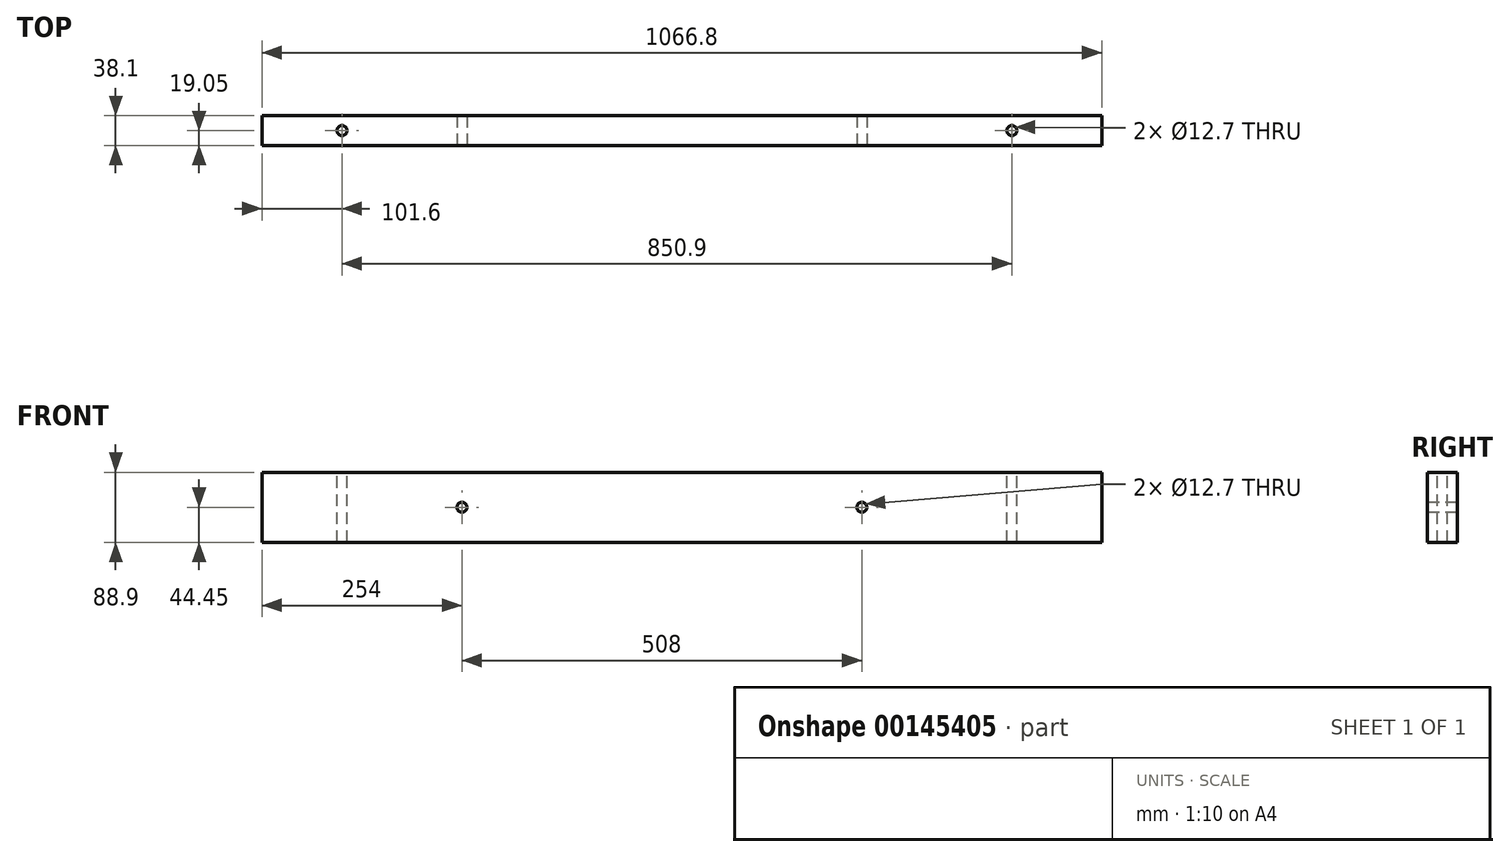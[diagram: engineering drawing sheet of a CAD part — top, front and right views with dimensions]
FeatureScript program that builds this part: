
annotation { "Feature Type Name" : "Feature", "Feature Type Description" : "" }
export const myFeature = defineFeature(function(context is Context, id is Id, definition is map)
    precondition{}
    {
        {
            var Q0;
            Q0=qCreatedBy(makeId("Front.planeOp"),FACE);
            var sketch = newSketch(context, id + "F0", { "sketchPlane" : qUnion([Q0])});
            skLineSegment(sketch, "E0.bottom", {"start": v(-533.4, -44.45) * mm, "end": v(533.4, -44.45) * mm});
            skLineSegment(sketch, "E0.top", {"start": v(-533.4, 44.45) * mm, "end": v(533.4, 44.45) * mm});
            skLineSegment(sketch, "E0.left", {"start": v(-533.4, -44.45) * mm, "end": v(-533.4, 44.45) * mm});
            skLineSegment(sketch, "E0.right", {"start": v(533.4, -44.45) * mm, "end": v(533.4, 44.45) * mm});
            skPoint(sketch, "E0.middle", {"position": v(0, 0) * mm});
            skPoint(sketch, "E1", {"position": v(-381, 0) * mm});
            skSolve(sketch);
        }
        {
            var Q0;
            Q0 = qSketchRegion(id + "F0", true);
            extrude(context, id + "F1", {"entities" : qUnion([Q0]), "endBound" : BoundingType.SYMMETRIC, "depth" : 38.1 * mm});
        }
        {
            var Q0;
            Q0=makeQuery(id+"F1.opExtrude","SWEPT_BODY",BODY,{"disambiguationData":[OSD([sQuery(id+"F0.wireOp",EDGE,"E0.bottom"),sQuery(id+"F0.wireOp",EDGE,"E0.top"),sQuery(id+"F0.wireOp",EDGE,"E0.left"),sQuery(id+"F0.wireOp",EDGE,"E0.right")])]});
            transform(context, id + "F2", {"entities" : qUnion([Q0]), "transformType" : TransformType.TRANSLATION_3D, "dx" : 0 * mm, "dy" : 114.3 * mm, "dz" : 0 * mm, "makeCopy" : true});
        }
        {
            var Q0;
            Q0=qCreatedBy(makeId("Front.planeOp"),FACE);
            var sketch = newSketch(context, id + "F3", { "sketchPlane" : qUnion([Q0])});
            skLineSegment(sketch, "E2.bottom", {"start": v(-190.5, 44.45) * mm, "end": v(190.5, 44.45) * mm});
            skLineSegment(sketch, "E2.top", {"start": v(-190.5, -44.45) * mm, "end": v(190.5, -44.45) * mm});
            skLineSegment(sketch, "E2.left", {"start": v(-190.5, 44.45) * mm, "end": v(-190.5, -44.45) * mm});
            skLineSegment(sketch, "E2.right", {"start": v(190.5, 44.45) * mm, "end": v(190.5, -44.45) * mm});
            skPoint(sketch, "E2.middle", {"position": v(0, 0) * mm});
            skSolve(sketch);
        }
        {
            var Q0;
            Q0 = qSketchRegion(id + "F3", true);
            extrude(context, id + "F4", {"entities" : qUnion([Q0]), "operationType" : NewBodyOperationType.ADD, "endBound" : BoundingType.SYMMETRIC, "depth" : 38.1 * mm});
        }
        {
            var Q0;
            Q0=makeQuery(id+"F2.opPattern","COPY",BODY,{"derivedFrom":makeQuery(id+"F1.opExtrude","SWEPT_BODY",BODY,{"disambiguationData":[OSD([sQuery(id+"F0.wireOp",EDGE,"E0.bottom"),sQuery(id+"F0.wireOp",EDGE,"E0.top"),sQuery(id+"F0.wireOp",EDGE,"E0.left"),sQuery(id+"F0.wireOp",EDGE,"E0.right")])]}),"instanceName":"1"});
            deleteBodies(context, id + "F5", {"entities" : qUnion([Q0])});
        }
        {
            var Q0;
            Q0=makeQuery(id+"F1.opExtrude","SWEPT_BODY",BODY,{"disambiguationData":[OSD([sQuery(id+"F0.wireOp",EDGE,"E0.bottom"),sQuery(id+"F0.wireOp",EDGE,"E0.top"),sQuery(id+"F0.wireOp",EDGE,"E0.left"),sQuery(id+"F0.wireOp",EDGE,"E0.right")])]});
            transform(context, id + "F6", {"entities" : qUnion([Q0]), "transformType" : TransformType.TRANSLATION_3D, "dx" : 0 * mm, "dy" : 152.4 * mm, "dz" : 0 * mm, "makeCopy" : true});
        }
        {
            var Q0;
            Q0=qCreatedBy(makeId("Front.planeOp"),FACE);
            cPlane(context, id + "F7", {"entities" : qUnion([Q0]), "cplaneType" : CPlaneType.OFFSET, "offset" : 91.44 * mm, "width" : 152.4 * mm, "height" : 152.4 * mm});
        }
        {
            var Q0;
            Q0=qCreatedBy(makeId("Top.planeOp"),FACE);
            cPlane(context, id + "F8", {"entities" : qUnion([Q0]), "cplaneType" : CPlaneType.OFFSET, "offset" : 152.4 * mm, "width" : 152.4 * mm, "height" : 152.4 * mm});
        }
        {
            var Q0;
            Q0=qCreatedBy(id+"F8.planeOp",FACE);
            var sketch = newSketch(context, id + "F9", { "sketchPlane" : qUnion([Q0])});
            skPoint(sketch, "E3", {"position": v(419.1, 0) * mm});
            skPoint(sketch, "E4", {"position": v(419.1, 152.4) * mm});
            skSolve(sketch);
        }
        {
            var Q0;
            Q0=sQuery(id+"F9.wireOp",VERTEX,"E4");
            var Q1;
            Q1=makeQuery(id+"F6.opPattern","COPY",BODY,{"derivedFrom":makeQuery(id+"F1.opExtrude","SWEPT_BODY",BODY,{"disambiguationData":[OSD([sQuery(id+"F0.wireOp",EDGE,"E0.bottom"),sQuery(id+"F0.wireOp",EDGE,"E0.top"),sQuery(id+"F0.wireOp",EDGE,"E0.left"),sQuery(id+"F0.wireOp",EDGE,"E0.right")])]}),"instanceName":"1"});
            hole(context, id + "F10", {"style" : HoleStyle.SIMPLE, "endStyle" : HoleEndStyle.BLIND, "holeDiameter" : 12.7 * mm, "holeDepth" : 609.6 * mm, "startFromSketch" : true, "locations" : qUnion([Q0]), "scope" : qUnion([Q1])});
        }
        {
            var Q0;
            Q0=sQuery(id+"F9.wireOp",VERTEX,"E3");
            var Q1;
            Q1=makeQuery(id+"F1.opExtrude","SWEPT_BODY",BODY,{"disambiguationData":[OSD([sQuery(id+"F0.wireOp",EDGE,"E0.bottom"),sQuery(id+"F0.wireOp",EDGE,"E0.top"),sQuery(id+"F0.wireOp",EDGE,"E0.left"),sQuery(id+"F0.wireOp",EDGE,"E0.right")])]});
            hole(context, id + "F11", {"style" : HoleStyle.SIMPLE, "endStyle" : HoleEndStyle.BLIND, "holeDiameter" : 12.7 * mm, "holeDepth" : 609.6 * mm, "startFromSketch" : true, "locations" : qUnion([Q0]), "scope" : qUnion([Q1])});
        }
        {
            var Q0;
            Q0=qCreatedBy(id+"F7.planeOp",FACE);
            var sketch = newSketch(context, id + "F12", { "sketchPlane" : qUnion([Q0])});
            skPoint(sketch, "E5", {"position": v(-279.4, 0) * mm});
            skSolve(sketch);
        }
        {
            var Q0;
            Q0=sQuery(id+"F12.wireOp",VERTEX,"E5");
            var Q1;
            Q1=makeQuery(id+"F1.opExtrude","SWEPT_BODY",BODY,{"disambiguationData":[OSD([sQuery(id+"F0.wireOp",EDGE,"E0.bottom"),sQuery(id+"F0.wireOp",EDGE,"E0.top"),sQuery(id+"F0.wireOp",EDGE,"E0.left"),sQuery(id+"F0.wireOp",EDGE,"E0.right")])]});
            var Q2;
            Q2=makeQuery(id+"F6.opPattern","COPY",BODY,{"derivedFrom":makeQuery(id+"F1.opExtrude","SWEPT_BODY",BODY,{"disambiguationData":[OSD([sQuery(id+"F0.wireOp",EDGE,"E0.bottom"),sQuery(id+"F0.wireOp",EDGE,"E0.top"),sQuery(id+"F0.wireOp",EDGE,"E0.left"),sQuery(id+"F0.wireOp",EDGE,"E0.right")])]}),"instanceName":"1"});
            hole(context, id + "F13", {"style" : HoleStyle.SIMPLE, "endStyle" : HoleEndStyle.BLIND, "holeDiameter" : 12.7 * mm, "holeDepth" : 609.6 * mm, "startFromSketch" : true, "locations" : qUnion([Q0]), "scope" : qUnion([Q1, Q2])});
        }
        {
            var Q0;
            Q0=makeQuery(id+"F6.opPattern","COPY",BODY,{"derivedFrom":makeQuery(id+"F1.opExtrude","SWEPT_BODY",BODY,{"disambiguationData":[OSD([sQuery(id+"F0.wireOp",EDGE,"E0.bottom"),sQuery(id+"F0.wireOp",EDGE,"E0.top"),sQuery(id+"F0.wireOp",EDGE,"E0.left"),sQuery(id+"F0.wireOp",EDGE,"E0.right")])]}),"instanceName":"1"});
            deleteBodies(context, id + "F14", {"entities" : qUnion([Q0])});
        }
        {
            var Q0;
            Q0=qCreatedBy(id+"F8.planeOp",FACE);
            var sketch = newSketch(context, id + "F15", { "sketchPlane" : qUnion([Q0])});
            skPoint(sketch, "E6", {"position": v(-431.8, 0) * mm});
            skSolve(sketch);
        }
        {
            var Q0;
            Q0=sQuery(id+"F15.wireOp",VERTEX,"E6");
            var Q1;
            Q1=makeQuery(id+"F1.opExtrude","SWEPT_BODY",BODY,{"disambiguationData":[OSD([sQuery(id+"F0.wireOp",EDGE,"E0.bottom"),sQuery(id+"F0.wireOp",EDGE,"E0.top"),sQuery(id+"F0.wireOp",EDGE,"E0.left"),sQuery(id+"F0.wireOp",EDGE,"E0.right")])]});
            hole(context, id + "F16", {"style" : HoleStyle.SIMPLE, "endStyle" : HoleEndStyle.BLIND, "holeDiameter" : 12.7 * mm, "holeDepth" : 609.6 * mm, "locations" : qUnion([Q0]), "scope" : qUnion([Q1])});
        }
        {
            var Q0;
            Q0=makeQuery(id+"F1.opExtrude","CAP_FACE",FACE,{"disambiguationData":[OSD([sQuery(id+"F0.wireOp",EDGE,"E0.bottom"),sQuery(id+"F0.wireOp",EDGE,"E0.top"),sQuery(id+"F0.wireOp",EDGE,"E0.left"),sQuery(id+"F0.wireOp",EDGE,"E0.right")])],"isStart":false});
            var sketch = newSketch(context, id + "F17", { "sketchPlane" : qUnion([Q0])});
            skPoint(sketch, "E7", {"position": v(228.6, 0) * mm});
            skSolve(sketch);
        }
        {
            var Q0;
            Q0=sQuery(id+"F17.wireOp",VERTEX,"E7");
            var Q1;
            Q1=makeQuery(id+"F1.opExtrude","SWEPT_BODY",BODY,{"disambiguationData":[OSD([sQuery(id+"F0.wireOp",EDGE,"E0.bottom"),sQuery(id+"F0.wireOp",EDGE,"E0.top"),sQuery(id+"F0.wireOp",EDGE,"E0.left"),sQuery(id+"F0.wireOp",EDGE,"E0.right")])]});
            hole(context, id + "F18", {"style" : HoleStyle.SIMPLE, "endStyle" : HoleEndStyle.BLIND, "holeDiameter" : 12.7 * mm, "holeDepth" : 609.6 * mm, "startFromSketch" : true, "locations" : qUnion([Q0]), "scope" : qUnion([Q1])});
        }
    });
